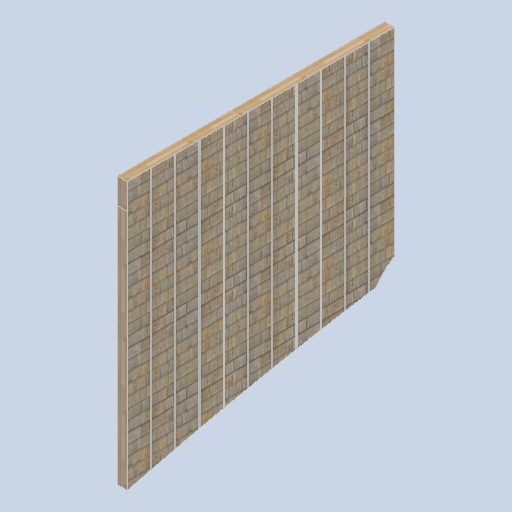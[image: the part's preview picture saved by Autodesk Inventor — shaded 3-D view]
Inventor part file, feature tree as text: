
AUTODESK INVENTOR PART (.ipt)
format: ipt  version: 2024.2 (Build 282272000, 272)  size: 330,752 bytes
history: native  units: in
note: dims shown in document units (in); Inventor stores cm internally (conversion verified against a paired STEP export)
features: other x3, sketch x2
ambient origin geometry x8: Origin, YZ Plane, XZ Plane, XY Plane, X Axis, Y Axis, Z Axis, Center Point
bodies: Solid1 (feature_tree)
feature tree (5):
  other  "side_wall_01.ipt"
  other  "Solid1::side_wall_01.ipt"
  other  "TaggingFeature1"
  sketch  "Sketch1"  dims[d0=0.3937in]
  sketch  "Sketch2"
